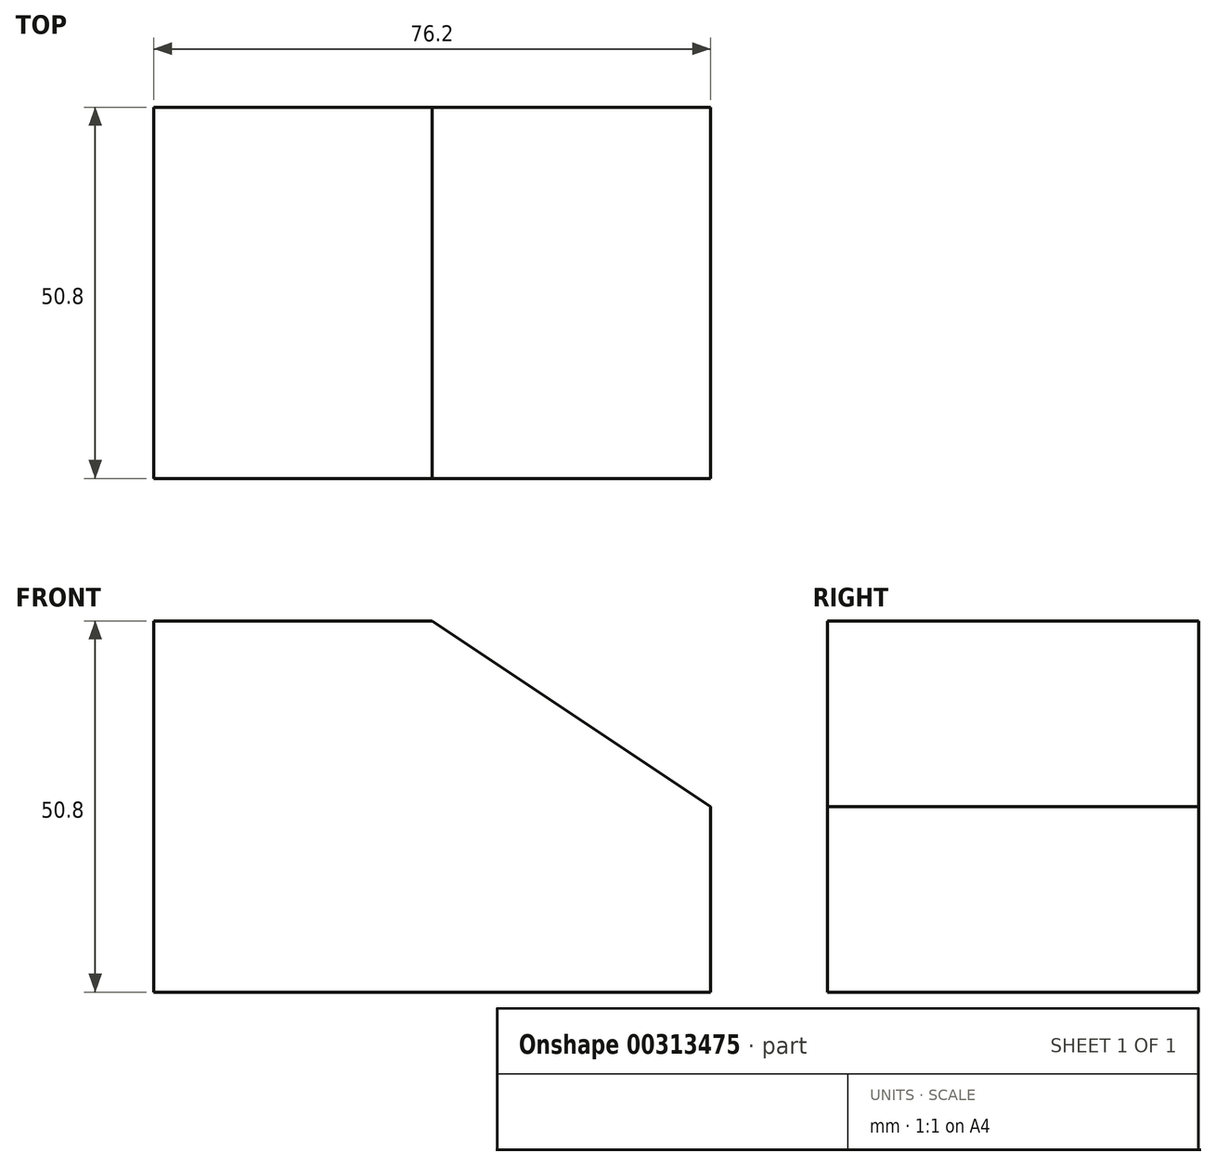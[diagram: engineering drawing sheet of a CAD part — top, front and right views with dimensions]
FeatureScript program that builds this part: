
annotation { "Feature Type Name" : "Feature", "Feature Type Description" : "" }
export const myFeature = defineFeature(function(context is Context, id is Id, definition is map)
    precondition{}
    {
        {
            var Q0;
            Q0=qCreatedBy(makeId("Front.planeOp"),FACE);
            var sketch = newSketch(context, id + "F0", { "sketchPlane" : qUnion([Q0])});
            skLineSegment(sketch, "E0", {"start": v(-31.59, -40.93) * mm, "end": v(44.61, -40.93) * mm});
            skLineSegment(sketch, "E1", {"start": v(44.61, -40.93) * mm, "end": v(44.61, -15.53) * mm});
            skLineSegment(sketch, "E2", {"start": v(6.51, 9.87) * mm, "end": v(-31.59, 9.87) * mm});
            skLineSegment(sketch, "E3", {"start": v(-31.59, 9.87) * mm, "end": v(-31.59, -40.93) * mm});
            skLineSegment(sketch, "E4", {"start": v(6.51, 9.87) * mm, "end": v(44.61, -15.53) * mm});
            skSolve(sketch);
        }
        {
            var Q0;
            Q0 = qSketchRegion(id + "F0", true);
            extrude(context, id + "F1", {"entities" : qUnion([Q0]), "depth" : 50.8 * mm});
        }
    });
